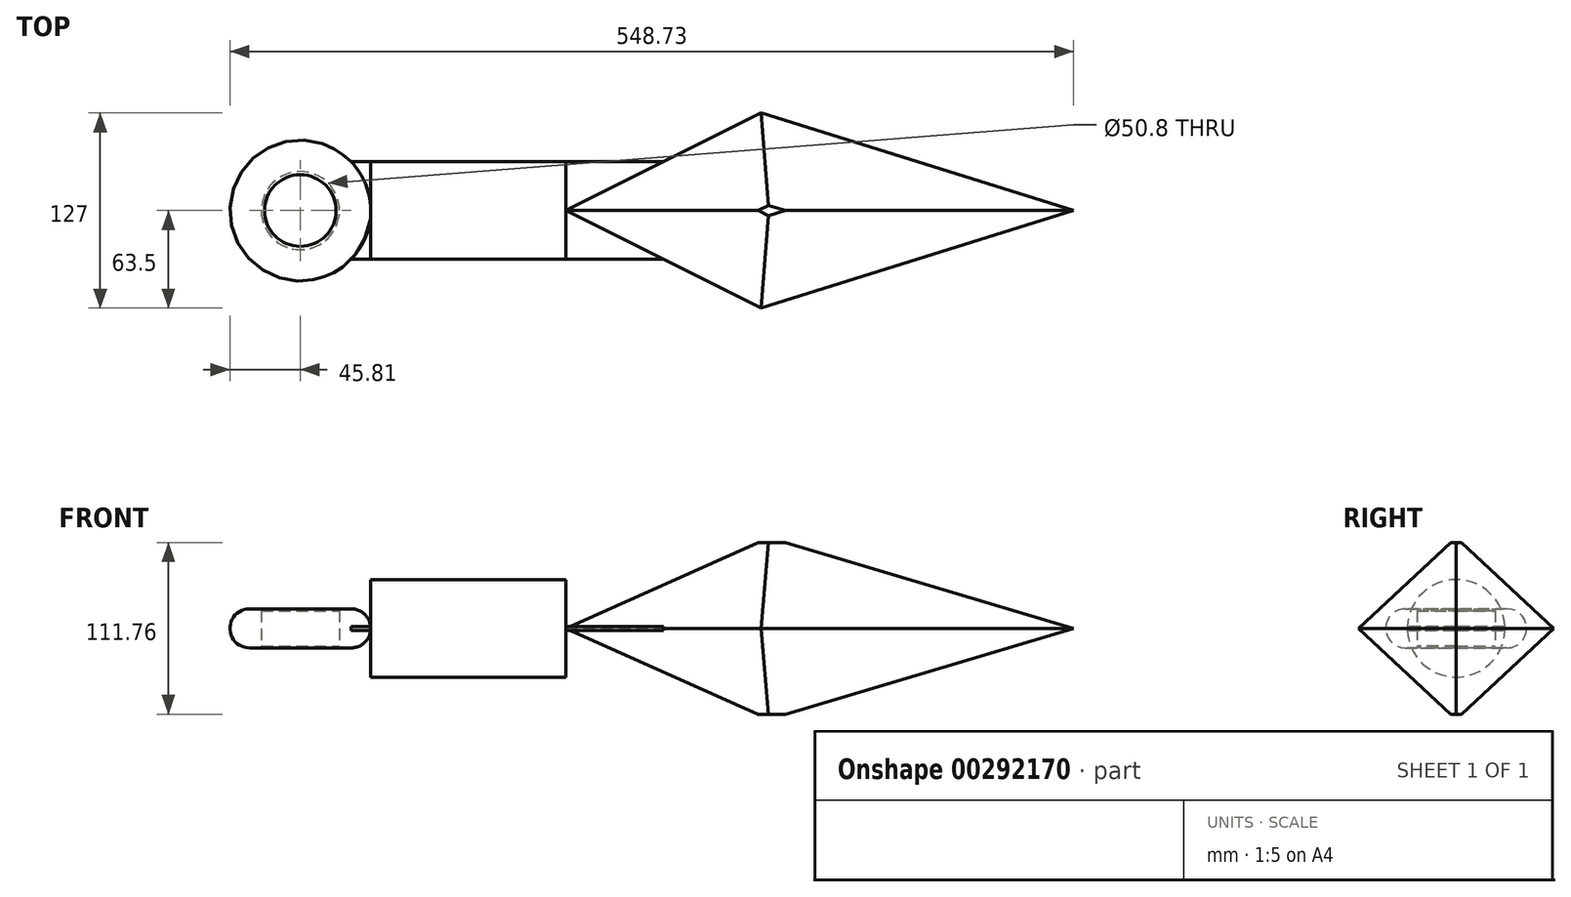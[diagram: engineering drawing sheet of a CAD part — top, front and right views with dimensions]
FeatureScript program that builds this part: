
annotation { "Feature Type Name" : "Feature", "Feature Type Description" : "" }
export const myFeature = defineFeature(function(context is Context, id is Id, definition is map)
    precondition{}
    {
        {
            var Q0;
            Q0=qCreatedBy(makeId("Top.planeOp"),FACE);
            var sketch = newSketch(context, id + "F0", { "sketchPlane" : qUnion([Q0])});
            skLineSegment(sketch, "E0", {"start": v(0, 0) * mm, "end": v(0, 63.5) * mm});
            skLineSegment(sketch, "E1", {"start": v(0, 0) * mm, "end": v(0, -63.5) * mm});
            skLineSegment(sketch, "E2", {"start": v(0, 0) * mm, "end": v(-127, 0) * mm});
            skLineSegment(sketch, "E3", {"start": v(0, 0) * mm, "end": v(203.2, 0) * mm});
            skLineSegment(sketch, "E4", {"start": v(0, 63.5) * mm, "end": v(-127, 0) * mm});
            skLineSegment(sketch, "E5", {"start": v(-127, 0) * mm, "end": v(0, -63.5) * mm});
            skLineSegment(sketch, "E6", {"start": v(0, -63.5) * mm, "end": v(203.2, 0) * mm});
            skLineSegment(sketch, "E7", {"start": v(203.2, 0) * mm, "end": v(0, 63.5) * mm});
            skLineSegment(sketch, "E8", {"start": v(-63.5, 31.75) * mm, "end": v(-266.7, 31.75) * mm});
            skLineSegment(sketch, "E9", {"start": v(-63.5, -31.75) * mm, "end": v(-266.7, -31.75) * mm});
            skPoint(sketch, "E10", {"position": v(-299.72, 0) * mm});
            skPoint(sketch, "E10.positionSnap0", {"position": v(-304.8, 63.5) * mm});
            skCircle(sketch, "E11", {"center": v(-299.72, 0) * mm, "radius": 45.8 * mm});
            skLineSegment(sketch, "E12", {"start": v(-127, 0) * mm, "end": v(-127, 31.75) * mm});
            skLineSegment(sketch, "E13", {"start": v(-127, 0) * mm, "end": v(-127, -31.75) * mm});
            skPoint(sketch, "E14", {"position": v(-253.91, 0) * mm});
            skLineSegment(sketch, "E15", {"start": v(-253.91, 0) * mm, "end": v(-253.91, 31.75) * mm});
            skLineSegment(sketch, "E16", {"start": v(-253.91, 0) * mm, "end": v(-253.91, -31.75) * mm});
            skLineSegment(sketch, "E17", {"start": v(-127, 0) * mm, "end": v(-253.91, 0) * mm});
            skSolve(sketch);
        }
        {
            var Q0;
            {var subQ0=sQuery(id+"F0.wireOp",EDGE,"E0");Q0=makeQuery(id+"F0.imprint","IMPRINT",FACE,{"disambiguationData":[TD([[makeQuery(id+"F0.imprint","IMPRINT",EDGE,{"derivedFrom":subQ0}),1.0]])]});}
            var Q1;
            Q1=makeQuery(id+"F0.imprint","IMPRINT",FACE,{"disambiguationData":[TD([[makeQuery(id+"F0.imprint","IMPRINT",EDGE,{"derivedFrom":sQuery(id+"F0.wireOp",EDGE,"E0")}),-1.0]])]});
            var Q2;
            Q2=makeQuery(id+"F0.imprint","IMPRINT",FACE,{"disambiguationData":[TD([[makeQuery(id+"F0.imprint","IMPRINT",EDGE,{"derivedFrom":sQuery(id+"F0.wireOp",EDGE,"E1")}),1.0]])]});
            var Q3;
            {var subQ0=sQuery(id+"F0.wireOp",EDGE,"E1");Q3=makeQuery(id+"F0.imprint","IMPRINT",FACE,{"disambiguationData":[TD([[makeQuery(id+"F0.imprint","IMPRINT",EDGE,{"derivedFrom":subQ0}),-1.0]])]});}
            extrude(context, id + "F1", {"entities" : qUnion([Q0, Q1, Q2, Q3]), "depth" : 55.88 * mm});
        }
        {
            var Q0;
            Q0=makeQuery(id+"F0.imprint","IMPRINT",FACE,{"disambiguationData":[TD([[makeQuery(id+"F0.imprint","IMPRINT",EDGE,{"derivedFrom":sQuery(id+"F0.wireOp",EDGE,"E0")}),-1.0]])]});
            var Q1;
            Q1=makeQuery(id+"F0.imprint","IMPRINT",FACE,{"disambiguationData":[TD([[makeQuery(id+"F0.imprint","IMPRINT",EDGE,{"derivedFrom":sQuery(id+"F0.wireOp",EDGE,"E1")}),1.0]])]});
            var Q2;
            {var subQ0=sQuery(id+"F0.wireOp",EDGE,"E0");Q2=makeQuery(id+"F0.imprint","IMPRINT",FACE,{"disambiguationData":[TD([[makeQuery(id+"F0.imprint","IMPRINT",EDGE,{"derivedFrom":subQ0}),1.0]])]});}
            var Q3;
            {var subQ0=sQuery(id+"F0.wireOp",EDGE,"E1");Q3=makeQuery(id+"F0.imprint","IMPRINT",FACE,{"disambiguationData":[TD([[makeQuery(id+"F0.imprint","IMPRINT",EDGE,{"derivedFrom":subQ0}),-1.0]])]});}
            extrude(context, id + "F2", {"entities" : qUnion([Q0, Q1, Q2, Q3]), "operationType" : NewBodyOperationType.ADD, "oppositeDirection" : true, "depth" : 55.88 * mm});
        }
        {
            var Q0;
            Q0=makeQuery(id+"F2.opExtrude","CAP_EDGE",EDGE,{"disambiguationData":[OSD([sQuery(id+"F0.wireOp",EDGE,"E6")])],"isStart":false});
            var Q1;
            Q1=makeQuery(id+"F2.opExtrude","CAP_EDGE",EDGE,{"disambiguationData":[OSD([sQuery(id+"F0.wireOp",EDGE,"E5")])],"isStart":false});
            var Q2;
            Q2=makeQuery(id+"F2.opExtrude","CAP_EDGE",EDGE,{"disambiguationData":[OSD([sQuery(id+"F0.wireOp",EDGE,"E4")])],"isStart":false});
            var Q3;
            Q3=makeQuery(id+"F2.opExtrude","CAP_EDGE",EDGE,{"disambiguationData":[OSD([sQuery(id+"F0.wireOp",EDGE,"E7")])],"isStart":false});
            chamfer(context, id + "F3", {"entities" : qUnion([Q0, Q1, Q2, Q3]), "width" : 55.88 * mm, "tangentPropagation" : true});
        }
        {
            var Q0;
            Q0=makeQuery(id+"F1.opExtrude","CAP_EDGE",EDGE,{"disambiguationData":[OSD([sQuery(id+"F0.wireOp",EDGE,"E4")])],"isStart":false});
            var Q1;
            Q1=makeQuery(id+"F1.opExtrude","CAP_EDGE",EDGE,{"disambiguationData":[OSD([sQuery(id+"F0.wireOp",EDGE,"E7")])],"isStart":false});
            var Q2;
            Q2=makeQuery(id+"F1.opExtrude","CAP_EDGE",EDGE,{"disambiguationData":[OSD([sQuery(id+"F0.wireOp",EDGE,"E6")])],"isStart":false});
            var Q3;
            Q3=makeQuery(id+"F1.opExtrude","CAP_EDGE",EDGE,{"disambiguationData":[OSD([sQuery(id+"F0.wireOp",EDGE,"E5")])],"isStart":false});
            chamfer(context, id + "F4", {"entities" : qUnion([Q0, Q1, Q2, Q3]), "width" : 55.88 * mm, "tangentPropagation" : true});
        }
        {
            var Q0;
            {var subQ0=sQuery(id+"F0.wireOp",EDGE,"E11");var subQ1=makeQuery(id+"F0.imprint","INTERSECT",VERTEX,{"derivedFrom":[sQuery(id+"F0.wireOp",EDGE,"E8"),subQ0]});Q0=makeQuery(id+"F0.imprint","IMPRINT",FACE,{"disambiguationData":[TD([[makeQuery(id+"F0.imprint","IMPRINT",EDGE,{"disambiguationData":[TD([[subQ1,-1.0]])],"derivedFrom":subQ0}),1.0]])]});}
            extrude(context, id + "F5", {"entities" : qUnion([Q0]), "depth" : 12.7 * mm});
        }
        {
            var Q0;
            {var subQ0=sQuery(id+"F0.wireOp",EDGE,"E11");var subQ1=makeQuery(id+"F0.imprint","INTERSECT",VERTEX,{"derivedFrom":[sQuery(id+"F0.wireOp",EDGE,"E8"),subQ0]});Q0=makeQuery(id+"F0.imprint","IMPRINT",FACE,{"disambiguationData":[TD([[makeQuery(id+"F0.imprint","IMPRINT",EDGE,{"disambiguationData":[TD([[subQ1,-1.0]])],"derivedFrom":subQ0}),1.0]])]});}
            extrude(context, id + "F6", {"entities" : qUnion([Q0]), "operationType" : NewBodyOperationType.ADD, "oppositeDirection" : true, "depth" : 12.7 * mm});
        }
        {
            var Q0;
            Q0=sQuery(id+"F0.wireOp",VERTEX,"E10");
            var Q1;
            Q1=makeQuery(id+"F5.opExtrude","SWEPT_BODY",BODY,{"disambiguationData":[OSD([sQuery(id+"F0.wireOp",EDGE,"E11")])]});
            hole(context, id + "F7", {"style" : HoleStyle.SIMPLE, "endStyle" : HoleEndStyle.BLIND, "oppositeDirection" : true, "holeDiameter" : 50.8 * mm, "holeDepth" : 11.43 * mm, "tappedDepth" : 12.7 * mm, "tapClearance" : 3, "locations" : qUnion([Q0]), "scope" : qUnion([Q1])});
        }
        {
            var Q0;
            Q0=sQuery(id+"F0.wireOp",VERTEX,"E10");
            var Q1;
            Q1=makeQuery(id+"F5.opExtrude","SWEPT_BODY",BODY,{"disambiguationData":[OSD([sQuery(id+"F0.wireOp",EDGE,"E11")])]});
            hole(context, id + "F8", {"style" : HoleStyle.SIMPLE, "endStyle" : HoleEndStyle.BLIND, "holeDiameter" : 50.8 * mm, "holeDepth" : 11.43 * mm, "tappedDepth" : 12.7 * mm, "tapClearance" : 3, "locations" : qUnion([Q0]), "scope" : qUnion([Q1])});
        }
        {
            var Q0;
            Q0=makeQuery(id+"F7.hole-0.boolean.opBoolean","INTERSECT",EDGE,{"derivedFrom":[makeQuery(id+"F5.opExtrude","CAP_FACE",FACE,{"disambiguationData":[OSD([sQuery(id+"F0.wireOp",EDGE,"E11")])],"isStart":false}),makeQuery(id+"F7.hole-0.opRevolve","SWEPT_FACE",FACE,{"disambiguationData":[OSD([sQuery(id+"F7.hole-0.sketch.wireOp",EDGE,"core_line_1")])]})]});
            var Q1;
            Q1=makeQuery(id+"F8.hole-0.boolean.opBoolean","INTERSECT",EDGE,{"derivedFrom":[makeQuery(id+"F6.opExtrude","CAP_FACE",FACE,{"disambiguationData":[OSD([sQuery(id+"F0.wireOp",EDGE,"E11")])],"isStart":false}),makeQuery(id+"F8.hole-0.opRevolve","SWEPT_FACE",FACE,{"disambiguationData":[OSD([sQuery(id+"F8.hole-0.sketch.wireOp",EDGE,"core_line_1")])]})]});
            var Q2;
            Q2=makeQuery(id+"F6.opExtrude","CAP_EDGE",EDGE,{"disambiguationData":[OSD([sQuery(id+"F0.wireOp",EDGE,"E11")])],"isStart":false});
            var Q3;
            Q3=makeQuery(id+"F5.opExtrude","CAP_EDGE",EDGE,{"disambiguationData":[OSD([sQuery(id+"F0.wireOp",EDGE,"E11")])],"isStart":false});
            fillet(context, id + "F9", {"entities" : qUnion([Q0, Q1, Q2, Q3]), "radius" : 12.7 * mm, "tangentPropagation" : true, "allowEdgeOverflow" : false});
        }
        {
            var Q0;
            {var subQ0=sQuery(id+"F0.wireOp",EDGE,"E12");Q0=makeQuery(id+"F0.imprint","IMPRINT",FACE,{"disambiguationData":[TD([[makeQuery(id+"F0.imprint","IMPRINT",EDGE,{"derivedFrom":subQ0}),1.0]])]});}
            var Q1;
            Q1=sQuery(id+"F0.wireOp",EDGE,"E17");
            revolve(context, id + "F10", {"entities" : qUnion([Q0]), "axis" : qUnion([Q1]), "revolveType" : RevolveType.FULL});
        }
        {
            var Q0;
            {var subQ0=sQuery(id+"F0.wireOp",EDGE,"E13");Q0=makeQuery(id+"F0.imprint","IMPRINT",FACE,{"disambiguationData":[TD([[makeQuery(id+"F0.imprint","IMPRINT",EDGE,{"derivedFrom":subQ0}),1.0]])]});}
            var Q1;
            {var subQ0=sQuery(id+"F0.wireOp",EDGE,"E12");Q1=makeQuery(id+"F0.imprint","IMPRINT",FACE,{"disambiguationData":[TD([[makeQuery(id+"F0.imprint","IMPRINT",EDGE,{"derivedFrom":subQ0}),-1.0]])]});}
            var Q2;
            {var subQ3=sQuery(id+"F0.wireOp",EDGE,"E16");Q2=makeQuery(id+"F0.imprint","IMPRINT",FACE,{"disambiguationData":[TD([[makeQuery(id+"F0.imprint","IMPRINT",EDGE,{"derivedFrom":subQ3}),-1.0]])]});}
            var Q3;
            {var subQ3=sQuery(id+"F0.wireOp",EDGE,"E15");Q3=makeQuery(id+"F0.imprint","IMPRINT",FACE,{"disambiguationData":[TD([[makeQuery(id+"F0.imprint","IMPRINT",EDGE,{"derivedFrom":subQ3}),1.0]])]});}
            extrude(context, id + "F11", {"entities" : qUnion([Q0, Q1, Q2, Q3]), "operationType" : NewBodyOperationType.ADD, "depth" : 1.27 * mm});
        }
        {
            var Q0;
            {var subQ0=sQuery(id+"F0.wireOp",EDGE,"E12");Q0=makeQuery(id+"F0.imprint","IMPRINT",FACE,{"disambiguationData":[TD([[makeQuery(id+"F0.imprint","IMPRINT",EDGE,{"derivedFrom":subQ0}),-1.0]])]});}
            var Q1;
            {var subQ0=sQuery(id+"F0.wireOp",EDGE,"E13");Q1=makeQuery(id+"F0.imprint","IMPRINT",FACE,{"disambiguationData":[TD([[makeQuery(id+"F0.imprint","IMPRINT",EDGE,{"derivedFrom":subQ0}),1.0]])]});}
            var Q2;
            {var subQ3=sQuery(id+"F0.wireOp",EDGE,"E15");Q2=makeQuery(id+"F0.imprint","IMPRINT",FACE,{"disambiguationData":[TD([[makeQuery(id+"F0.imprint","IMPRINT",EDGE,{"derivedFrom":subQ3}),1.0]])]});}
            var Q3;
            {var subQ3=sQuery(id+"F0.wireOp",EDGE,"E16");Q3=makeQuery(id+"F0.imprint","IMPRINT",FACE,{"disambiguationData":[TD([[makeQuery(id+"F0.imprint","IMPRINT",EDGE,{"derivedFrom":subQ3}),-1.0]])]});}
            extrude(context, id + "F12", {"entities" : qUnion([Q0, Q1, Q2, Q3]), "operationType" : NewBodyOperationType.ADD, "oppositeDirection" : true, "depth" : 1.27 * mm});
        }
    });
